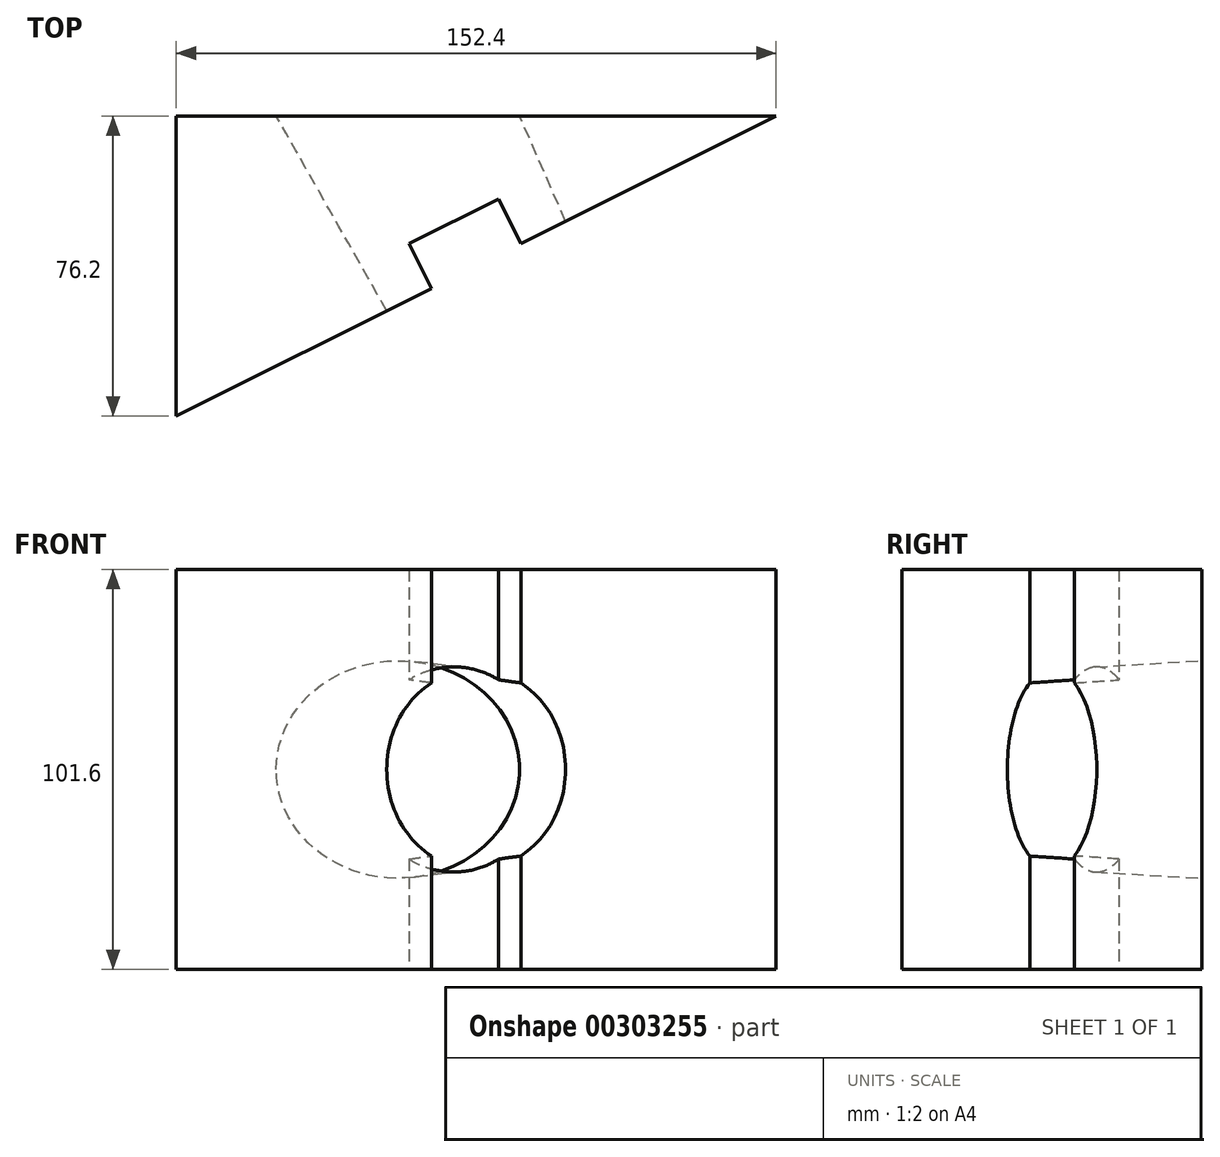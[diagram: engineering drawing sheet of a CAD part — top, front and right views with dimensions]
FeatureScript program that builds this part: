
annotation { "Feature Type Name" : "Feature", "Feature Type Description" : "" }
export const myFeature = defineFeature(function(context is Context, id is Id, definition is map)
    precondition{}
    {
        {
            var Q0;
            Q0=qCreatedBy(makeId("Top.planeOp"),FACE);
            var sketch = newSketch(context, id + "F0", { "sketchPlane" : qUnion([Q0])});
            skLineSegment(sketch, "E0.bottom", {"start": v(0, 0) * mm, "end": v(152.4, 0) * mm});
            skLineSegment(sketch, "E0.top", {"start": v(0, 76.2) * mm, "end": v(152.4, 76.2) * mm});
            skLineSegment(sketch, "E0.left", {"start": v(0, 0) * mm, "end": v(0, 76.2) * mm});
            skLineSegment(sketch, "E0.right", {"start": v(152.4, 0) * mm, "end": v(152.4, 76.2) * mm});
            skLineSegment(sketch, "E1", {"start": v(0, 0) * mm, "end": v(152.4, 76.2) * mm});
            skSolve(sketch);
        }
        {
            var Q0;
            Q0=makeQuery(id+"F0.imprint","IMPRINT",FACE,{"disambiguationData":[TD([[makeQuery(id+"F0.imprint","IMPRINT",EDGE,{"derivedFrom":sQuery(id+"F0.wireOp",EDGE,"E0.top")}),-1.0]])]});
            extrude(context, id + "F1", {"entities" : qUnion([Q0]), "depth" : 101.6 * mm});
        }
        {
            var Q0;
            Q0=makeQuery(id+"F1.opExtrude","SWEPT_FACE",FACE,{"disambiguationData":[OSD([sQuery(id+"F0.wireOp",EDGE,"E1")])]});
            var sketch = newSketch(context, id + "F2", { "sketchPlane" : qUnion([Q0])});
            skLineSegment(sketch, "E2.bottom", {"start": v(97.9, 101.6) * mm, "end": v(72.5, 101.6) * mm});
            skLineSegment(sketch, "E2.top", {"start": v(97.9, 0) * mm, "end": v(72.5, 0) * mm});
            skLineSegment(sketch, "E2.left", {"start": v(97.9, 101.6) * mm, "end": v(97.9, 0) * mm});
            skLineSegment(sketch, "E2.right", {"start": v(72.5, 101.6) * mm, "end": v(72.5, 0) * mm});
            skPoint(sketch, "E2.middle", {"position": v(85.2, 50.8) * mm});
            skPoint(sketch, "E2.middle.positionSnap0", {"position": v(170.39, 50.8) * mm});
            skPoint(sketch, "E2.middle.positionSnap1", {"position": v(85.2, 101.6) * mm});
            skPoint(sketch, "E2.centerSnap0", {"position": v(170.39, 50.8) * mm});
            skPoint(sketch, "E2.centerSnap1", {"position": v(85.2, 101.6) * mm});
            skSolve(sketch);
        }
        {
            var Q0;
            Q0=makeQuery(id+"F2.imprint","IMPRINT",FACE,{"disambiguationData":[TD([[makeQuery(id+"F2.imprint","IMPRINT",EDGE,{"derivedFrom":sQuery(id+"F2.wireOp",EDGE,"E2.bottom")}),-1.0]])]});
            extrude(context, id + "F3", {"entities" : qUnion([Q0]), "operationType" : NewBodyOperationType.REMOVE, "oppositeDirection" : true, "depth" : 12.7 * mm});
        }
        {
            var Q0;
            {var subQ0=sQuery(id+"F0.wireOp",EDGE,"E1");var subQ1=sQuery(id+"F0.wireOp",EDGE,"E0.left");Q0=makeQuery(id+"F3.boolean.opBoolean","SPLIT",FACE,{"disambiguationData":[TD([makeQuery(id+"F1.opExtrude","SWEPT_FACE",FACE,{"disambiguationData":[OSD([subQ1])]})])],"derivedFrom":makeQuery(id+"F1.opExtrude","SWEPT_FACE",FACE,{"disambiguationData":[OSD([subQ0])]})});}
            var sketch = newSketch(context, id + "F4", { "sketchPlane" : qUnion([Q0])});
            skCircle(sketch, "E3", {"center": v(85.2, 50.8) * mm, "radius": 25.4 * mm});
            skSolve(sketch);
        }
        {
            var Q0;
            {var subQ0=sQuery(id+"F4.wireOp",EDGE,"E3");var subQ1=makeQuery(id+"F3.boolean.opBoolean","COPY",EDGE,{"derivedFrom":makeQuery(id+"F3.opExtrude","CAP_EDGE",EDGE,{"disambiguationData":[OSD([sQuery(id+"F2.wireOp",EDGE,"E2.right")])],"isStart":true})});var subQ2=makeQuery(id+"F4.imprint","INTERSECT",VERTEX,{"disambiguationData":[OD(0.0)],"derivedFrom":[subQ1,subQ0]});Q0=makeQuery(id+"F4.imprint","IMPRINT",FACE,{"disambiguationData":[TD([[makeQuery(id+"F4.imprint","IMPRINT",EDGE,{"disambiguationData":[TD([[subQ2,1.0]])],"derivedFrom":subQ0}),1.0]])]});}
            var Q1;
            {var subQ0=sQuery(id+"F4.wireOp",EDGE,"E3");var subQ1=makeQuery(id+"F3.boolean.opBoolean","COPY",EDGE,{"derivedFrom":makeQuery(id+"F3.opExtrude","CAP_EDGE",EDGE,{"disambiguationData":[OSD([sQuery(id+"F2.wireOp",EDGE,"E2.right")])],"isStart":true})});var subQ2=makeQuery(id+"F4.imprint","INTERSECT",VERTEX,{"disambiguationData":[OD(0.0)],"derivedFrom":[subQ1,subQ0]});Q1=makeQuery(id+"F4.imprint","IMPRINT",FACE,{"disambiguationData":[TD([[makeQuery(id+"F4.imprint","IMPRINT",EDGE,{"disambiguationData":[TD([[subQ2,-1.0]])],"derivedFrom":subQ0}),1.0]])]});}
            var Q2;
            Q2=sQuery(id+"F4.wireOp",EDGE,"E3");
            extrude(context, id + "F5", {"entities" : qUnion([Q0, Q1]), "operationType" : NewBodyOperationType.REMOVE, "surfaceEntities" : qUnion([Q2]), "oppositeDirection" : true, "depth" : 141.48 * mm, "hasDraft" : true, "draftAngle" : 3 * degree});
        }
    });
